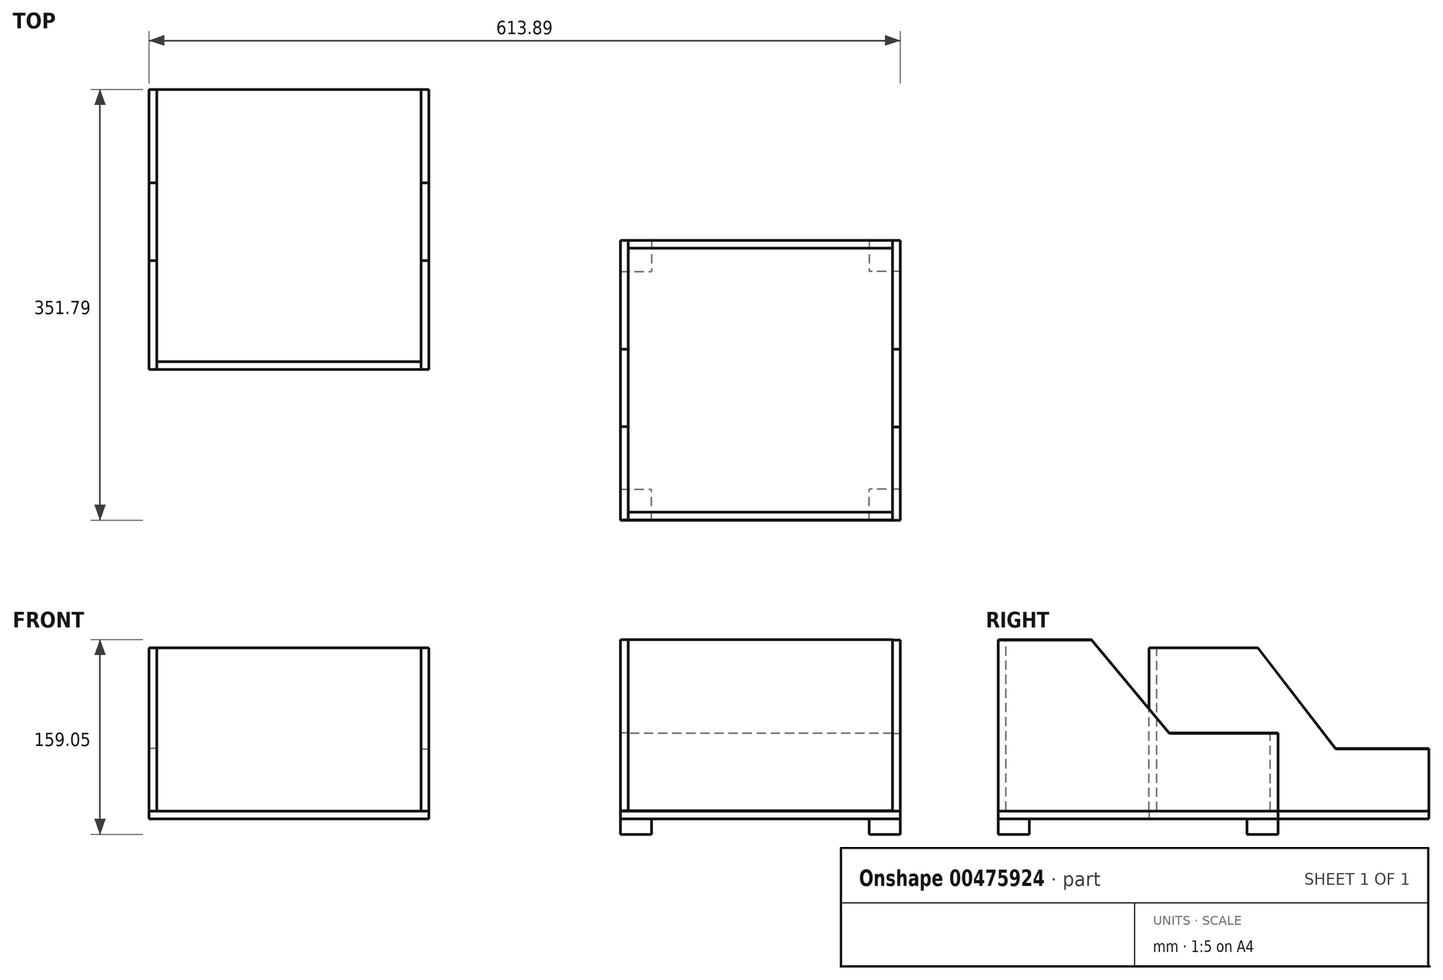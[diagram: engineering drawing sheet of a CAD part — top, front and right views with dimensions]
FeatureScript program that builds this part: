
annotation { "Feature Type Name" : "Feature", "Feature Type Description" : "" }
export const myFeature = defineFeature(function(context is Context, id is Id, definition is map)
    precondition{}
    {
        {
            var Q0;
            Q0=qCreatedBy(makeId("Top.planeOp"),FACE);
            var sketch = newSketch(context, id + "F0", { "sketchPlane" : qUnion([Q0])});
            skLineSegment(sketch, "E0.bottom", {"start": v(0, 0) * mm, "end": v(228.6, 0) * mm});
            skLineSegment(sketch, "E0.top", {"start": v(0, -228.6) * mm, "end": v(228.6, -228.6) * mm});
            skLineSegment(sketch, "E0.left", {"start": v(0, 0) * mm, "end": v(0, -228.6) * mm});
            skLineSegment(sketch, "E0.right", {"start": v(228.6, 0) * mm, "end": v(228.6, -228.6) * mm});
            skSolve(sketch);
        }
        {
            var Q0;
            Q0=makeQuery(id+"F0.imprint","IMPRINT",FACE,{"disambiguationData":[TD([[makeQuery(id+"F0.imprint","IMPRINT",EDGE,{"derivedFrom":sQuery(id+"F0.wireOp",EDGE,"E0.bottom")}),-1.0]])]});
            extrude(context, id + "F1", {"entities" : qUnion([Q0]), "depth" : 6.35 * mm});
        }
        {
            var Q0;
            Q0=makeQuery(id+"F1.opExtrude","CAP_FACE",FACE,{"disambiguationData":[OSD([sQuery(id+"F0.wireOp",EDGE,"E0.bottom"),sQuery(id+"F0.wireOp",EDGE,"E0.top"),sQuery(id+"F0.wireOp",EDGE,"E0.left"),sQuery(id+"F0.wireOp",EDGE,"E0.right")])],"isStart":true});
            var sketch = newSketch(context, id + "F2", { "sketchPlane" : qUnion([Q0])});
            skLineSegment(sketch, "E1.bottom", {"start": v(0, 228.6) * mm, "end": v(25.4, 228.6) * mm});
            skLineSegment(sketch, "E1.top", {"start": v(0, 203.2) * mm, "end": v(25.4, 203.2) * mm});
            skLineSegment(sketch, "E1.left", {"start": v(0, 228.6) * mm, "end": v(0, 203.2) * mm});
            skLineSegment(sketch, "E1.right", {"start": v(25.4, 228.6) * mm, "end": v(25.4, 203.2) * mm});
            skLineSegment(sketch, "E2.bottom", {"start": v(228.6, 228.6) * mm, "end": v(203.2, 228.6) * mm});
            skLineSegment(sketch, "E2.top", {"start": v(228.6, 203.2) * mm, "end": v(203.2, 203.2) * mm});
            skLineSegment(sketch, "E2.left", {"start": v(228.6, 228.6) * mm, "end": v(228.6, 203.2) * mm});
            skLineSegment(sketch, "E2.right", {"start": v(203.2, 228.6) * mm, "end": v(203.2, 203.2) * mm});
            skLineSegment(sketch, "E3.bottom", {"start": v(0, 0) * mm, "end": v(25.4, 0) * mm});
            skLineSegment(sketch, "E3.top", {"start": v(0, 25.4) * mm, "end": v(25.4, 25.4) * mm});
            skLineSegment(sketch, "E3.left", {"start": v(0, 0) * mm, "end": v(0, 25.4) * mm});
            skLineSegment(sketch, "E3.right", {"start": v(25.4, 0) * mm, "end": v(25.4, 25.4) * mm});
            skLineSegment(sketch, "E4.bottom", {"start": v(228.6, 0) * mm, "end": v(203.2, 0) * mm});
            skLineSegment(sketch, "E4.top", {"start": v(228.6, 25.4) * mm, "end": v(203.2, 25.4) * mm});
            skLineSegment(sketch, "E4.left", {"start": v(228.6, 0) * mm, "end": v(228.6, 25.4) * mm});
            skLineSegment(sketch, "E4.right", {"start": v(203.2, 0) * mm, "end": v(203.2, 25.4) * mm});
            skSolve(sketch);
        }
        {
            var Q0;
            Q0 = qSketchRegion(id + "F2", true);
            var Q1;
            Q1 = qSketchRegion(id + "F3zAi2tQXCX8Qot_1", true);
            extrude(context, id + "F3", {"entities" : qUnion([Q0, Q1]), "depth" : 12.7 * mm});
        }
        {
            var Q0;
            Q0=qCreatedBy(makeId("Right.planeOp"),FACE);
            var sketch = newSketch(context, id + "F4", { "sketchPlane" : qUnion([Q0])});
            skLineSegment(sketch, "E5", {"start": v(-228.51, 6.65) * mm, "end": v(-228.51, 146.35) * mm});
            skLineSegment(sketch, "E6", {"start": v(0, 6.42) * mm, "end": v(0, 69.92) * mm});
            skLineSegment(sketch, "E7", {"start": v(0, 69.92) * mm, "end": v(-88.9, 69.92) * mm});
            skLineSegment(sketch, "E8", {"start": v(-228.51, 146.35) * mm, "end": v(-152.31, 146.35) * mm});
            skLineSegment(sketch, "E9", {"start": v(-152.31, 146.35) * mm, "end": v(-88.9, 69.92) * mm});
            skLineSegment(sketch, "E10", {"start": v(0, 6.42) * mm, "end": v(-228.51, 6.65) * mm});
            skSolve(sketch);
        }
        {
            var Q0;
            Q0 = qSketchRegion(id + "F4", true);
            extrude(context, id + "F5", {"entities" : qUnion([Q0]), "depth" : 6.35 * mm});
        }
        {
            var Q0;
            Q0=makeQuery(id+"F3.boolean.opBoolean","MERGE",FACE,{"derivedFrom":[makeQuery(id+"F1.opExtrude","SWEPT_FACE",FACE,{"disambiguationData":[OSD([sQuery(id+"F0.wireOp",EDGE,"E0.right")])]}),makeQuery(id+"F3.opExtrude","SWEPT_FACE",FACE,{"disambiguationData":[OSD([sQuery(id+"F2.wireOp",EDGE,"E2.left")])]}),makeQuery(id+"F3.opExtrude","SWEPT_FACE",FACE,{"disambiguationData":[OSD([sQuery(id+"F2.wireOp",EDGE,"E4.left")])]})]});
            var sketch = newSketch(context, id + "F6", { "sketchPlane" : qUnion([Q0])});
            skLineSegment(sketch, "E11", {"start": v(0, 6.35) * mm, "end": v(0, 69.85) * mm});
            skLineSegment(sketch, "E12", {"start": v(0, 69.85) * mm, "end": v(-88.9, 69.85) * mm});
            skLineSegment(sketch, "E13", {"start": v(-228.6, 6.35) * mm, "end": v(-228.6, 146.05) * mm});
            skLineSegment(sketch, "E14", {"start": v(-228.6, 146.05) * mm, "end": v(-152.4, 146.05) * mm});
            skLineSegment(sketch, "E15", {"start": v(-152.4, 146.05) * mm, "end": v(-88.9, 69.85) * mm});
            skLineSegment(sketch, "E16", {"start": v(-228.6, 6.35) * mm, "end": v(0, 6.35) * mm});
            skSolve(sketch);
        }
        {
            var Q0;
            Q0=makeQuery(id+"F6.imprint","IMPRINT",FACE,{"disambiguationData":[TD([[makeQuery(id+"F6.imprint","IMPRINT",EDGE,{"derivedFrom":sQuery(id+"F6.wireOp",EDGE,"E11")}),1.0]])]});
            extrude(context, id + "F7", {"entities" : qUnion([Q0]), "oppositeDirection" : true, "depth" : 6.35 * mm});
        }
        {
            var Q0;
            Q0=qCreatedBy(makeId("Front.planeOp"),FACE);
            var sketch = newSketch(context, id + "F8", { "sketchPlane" : qUnion([Q0])});
            skLineSegment(sketch, "E17", {"start": v(222.2, 69.78) * mm, "end": v(6.3, 69.78) * mm});
            skLineSegment(sketch, "E18", {"start": v(6.3, 6.2) * mm, "end": v(222.2, 6.2) * mm});
            skLineSegment(sketch, "E19", {"start": v(222.2, 6.2) * mm, "end": v(222.2, 69.78) * mm});
            skLineSegment(sketch, "E20", {"start": v(6.3, 69.78) * mm, "end": v(6.3, 6.2) * mm});
            skSolve(sketch);
        }
        {
            var Q0;
            Q0 = qSketchRegion(id + "F8", true);
            extrude(context, id + "F9", {"entities" : qUnion([Q0]), "depth" : 6.35 * mm});
        }
        {
            var Q0;
            Q0=makeQuery(id+"F5.opExtrude","SWEPT_FACE",FACE,{"disambiguationData":[OSD([sQuery(id+"F4.wireOp",EDGE,"E5")])]});
            var sketch = newSketch(context, id + "F10", { "sketchPlane" : qUnion([Q0])});
            skLineSegment(sketch, "E21", {"start": v(6.35, 146.35) * mm, "end": v(222.25, 146.35) * mm});
            skLineSegment(sketch, "E22", {"start": v(6.35, 146.35) * mm, "end": v(6.35, 6.65) * mm});
            skLineSegment(sketch, "E23", {"start": v(222.25, 6.65) * mm, "end": v(222.25, 146.35) * mm});
            skLineSegment(sketch, "E24", {"start": v(6.35, 6.65) * mm, "end": v(222.25, 6.65) * mm});
            skSolve(sketch);
        }
        {
            var Q0;
            Q0 = qSketchRegion(id + "F10", true);
            extrude(context, id + "F11", {"entities" : qUnion([Q0]), "oppositeDirection" : true, "depth" : 6.35 * mm});
        }
        {
            var Q0;
            Q0=qCreatedBy(makeId("Top.planeOp"),FACE);
            var sketch = newSketch(context, id + "F12", { "sketchPlane" : qUnion([Q0])});
            skLineSegment(sketch, "E25.bottom", {"start": v(-156.69, 122.98) * mm, "end": v(-385.29, 122.98) * mm});
            skLineSegment(sketch, "E25.top", {"start": v(-156.69, -105.62) * mm, "end": v(-385.29, -105.62) * mm});
            skLineSegment(sketch, "E25.left", {"start": v(-156.69, 122.98) * mm, "end": v(-156.69, -105.62) * mm});
            skLineSegment(sketch, "E25.right", {"start": v(-385.29, 122.98) * mm, "end": v(-385.29, -105.62) * mm});
            skSolve(sketch);
        }
        {
            var Q0;
            Q0=makeQuery(id+"F12.imprint","IMPRINT",FACE,{"disambiguationData":[TD([[makeQuery(id+"F12.imprint","IMPRINT",EDGE,{"derivedFrom":sQuery(id+"F12.wireOp",EDGE,"E25.bottom")}),1.0]])]});
            extrude(context, id + "F13", {"entities" : qUnion([Q0]), "depth" : 6.35 * mm});
        }
        {
            var Q0;
            Q0=makeQuery(id+"F13.opExtrude","SWEPT_FACE",FACE,{"disambiguationData":[OSD([sQuery(id+"F12.wireOp",EDGE,"E25.right")])]});
            var sketch = newSketch(context, id + "F14", { "sketchPlane" : qUnion([Q0])});
            skLineSegment(sketch, "E26", {"start": v(-123.19, 57.45) * mm, "end": v(-46.99, 57.45) * mm});
            skLineSegment(sketch, "E27", {"start": v(-123.19, 57.45) * mm, "end": v(-122.98, 6.35) * mm});
            skLineSegment(sketch, "E28", {"start": v(-122.98, 6.35) * mm, "end": v(105.62, 6.35) * mm});
            skLineSegment(sketch, "E29", {"start": v(105.62, 6.35) * mm, "end": v(105.62, 139.7) * mm});
            skLineSegment(sketch, "E30", {"start": v(105.62, 139.7) * mm, "end": v(16.72, 139.7) * mm});
            skLineSegment(sketch, "E31", {"start": v(16.72, 139.7) * mm, "end": v(-46.99, 57.45) * mm});
            skSolve(sketch);
        }
        {
            var Q0;
            Q0=makeQuery(id+"F14.imprint","IMPRINT",FACE,{"disambiguationData":[TD([[makeQuery(id+"F14.imprint","IMPRINT",EDGE,{"derivedFrom":sQuery(id+"F14.wireOp",EDGE,"E26")}),-1.0]])]});
            extrude(context, id + "F15", {"entities" : qUnion([Q0]), "oppositeDirection" : true, "depth" : 6.35 * mm});
        }
        {
            var Q0;
            Q0=makeQuery(id+"F13.opExtrude","SWEPT_FACE",FACE,{"disambiguationData":[OSD([sQuery(id+"F12.wireOp",EDGE,"E25.left")])]});
            var sketch = newSketch(context, id + "F16", { "sketchPlane" : qUnion([Q0])});
            skLineSegment(sketch, "E32", {"start": v(122.98, 6.35) * mm, "end": v(122.98, 57.15) * mm});
            skLineSegment(sketch, "E33", {"start": v(122.98, 57.15) * mm, "end": v(46.78, 57.15) * mm});
            skLineSegment(sketch, "E34", {"start": v(-105.62, 6.35) * mm, "end": v(-105.62, 139.7) * mm});
            skLineSegment(sketch, "E35", {"start": v(-105.62, 139.7) * mm, "end": v(-16.72, 139.7) * mm});
            skLineSegment(sketch, "E36", {"start": v(-16.72, 139.7) * mm, "end": v(46.78, 57.15) * mm});
            skSolve(sketch);
        }
        {
            var Q0;
            Q0=makeQuery(id+"F16.imprint","IMPRINT",FACE,{"disambiguationData":[TD([[makeQuery(id+"F16.imprint","IMPRINT",EDGE,{"derivedFrom":sQuery(id+"F16.wireOp",EDGE,"E32")}),1.0]])]});
            extrude(context, id + "F17", {"entities" : qUnion([Q0]), "oppositeDirection" : true, "depth" : 6.35 * mm});
        }
        {
            var Q0;
            Q0=makeQuery(id+"F13.opExtrude","SWEPT_FACE",FACE,{"disambiguationData":[OSD([sQuery(id+"F12.wireOp",EDGE,"E25.top")])]});
            var sketch = newSketch(context, id + "F18", { "sketchPlane" : qUnion([Q0])});
            skLineSegment(sketch, "E37", {"start": v(-163.04, 6.35) * mm, "end": v(-378.94, 6.35) * mm});
            skLineSegment(sketch, "E38", {"start": v(-378.94, 6.35) * mm, "end": v(-378.94, 139.7) * mm});
            skLineSegment(sketch, "E39", {"start": v(-163.04, 6.35) * mm, "end": v(-163.04, 139.7) * mm});
            skLineSegment(sketch, "E40", {"start": v(-163.04, 139.7) * mm, "end": v(-378.94, 139.7) * mm});
            skSolve(sketch);
        }
        {
            var Q0;
            Q0 = qSketchRegion(id + "F18", true);
            extrude(context, id + "F19", {"entities" : qUnion([Q0]), "oppositeDirection" : true, "depth" : 6.35 * mm});
        }
    });
